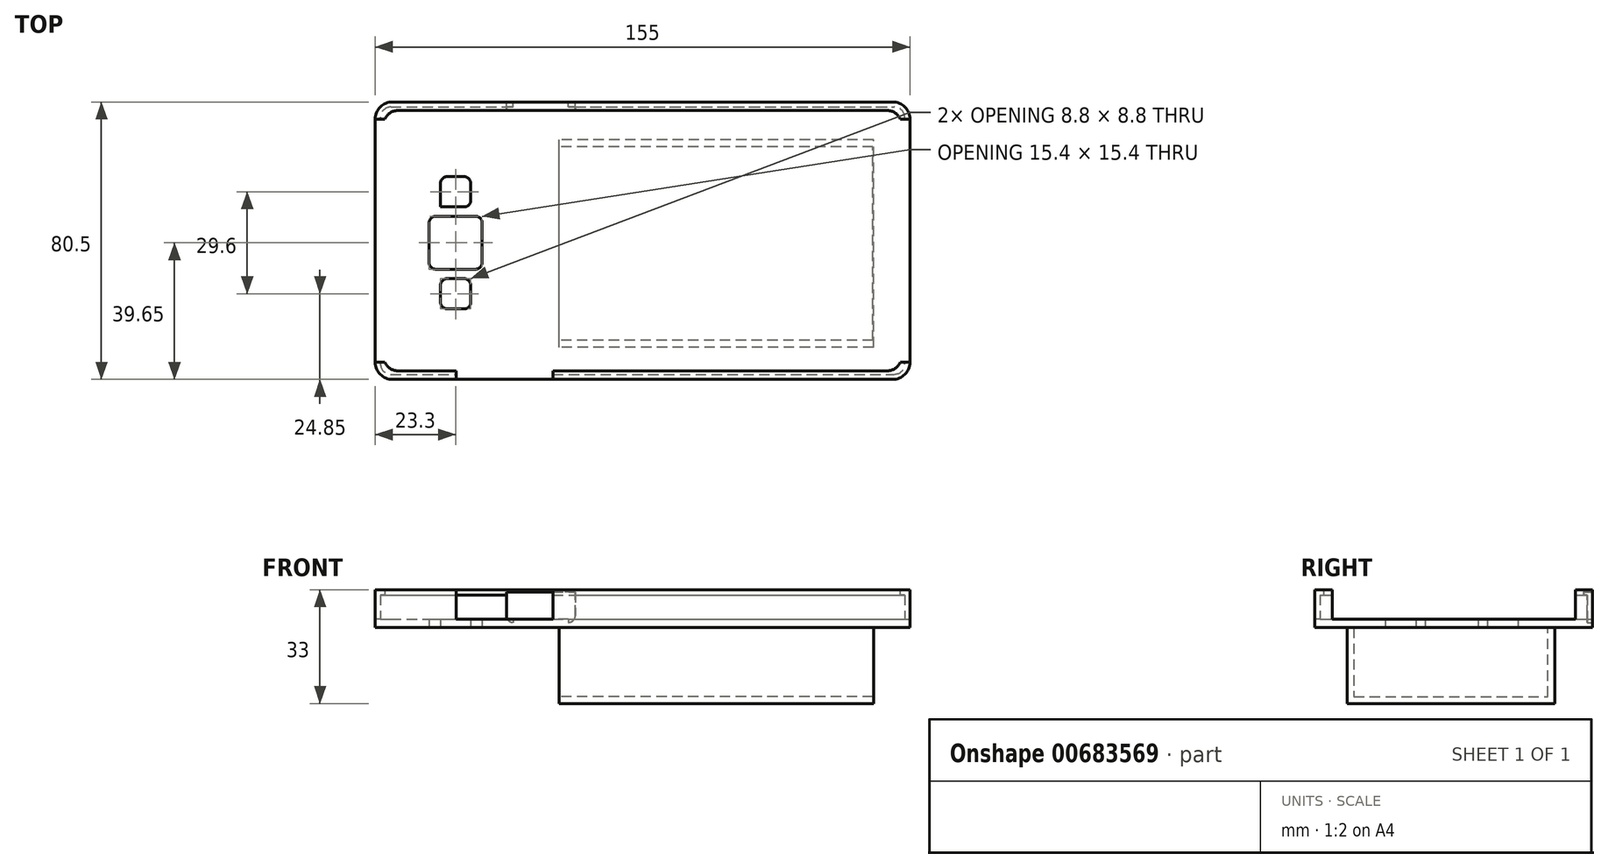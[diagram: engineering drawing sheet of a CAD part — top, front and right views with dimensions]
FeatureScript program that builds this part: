
annotation { "Feature Type Name" : "Feature", "Feature Type Description" : "" }
export const myFeature = defineFeature(function(context is Context, id is Id, definition is map)
    precondition{}
    {
        {
            var Q0;
            Q0=qCreatedBy(makeId("Top.planeOp"),FACE);
            var sketch = newSketch(context, id + "F0", { "sketchPlane" : qUnion([Q0])});
            skLineSegment(sketch, "E0.bottom", {"start": v(0, 0) * mm, "end": v(155, 0) * mm});
            skLineSegment(sketch, "E0.top", {"start": v(0, 80.5) * mm, "end": v(155, 80.5) * mm});
            skLineSegment(sketch, "E0.left", {"start": v(0, 0) * mm, "end": v(0, 80.5) * mm});
            skLineSegment(sketch, "E0.right", {"start": v(155, 0) * mm, "end": v(155, 80.5) * mm});
            skSolve(sketch);
        }
        {
            var Q0;
            Q0=qSketchRegion(id+"F0",true);
            extrude(context, id + "F1", {"entities" : qUnion([Q0]), "depth" : 9.5 * mm, "offsetDistance" : 25 * mm});
        }
        {
            var Q0;
            Q0=makeQuery(id+"F1.opExtrude","CAP_FACE",FACE,{"disambiguationData":[OSD([sQuery(id+"F0.wireOp",EDGE,"E0.bottom"),sQuery(id+"F0.wireOp",EDGE,"E0.top"),sQuery(id+"F0.wireOp",EDGE,"E0.left"),sQuery(id+"F0.wireOp",EDGE,"E0.right")])],"isStart":false});
            shell(context, id + "F2", {"entities" : qUnion([Q0]), "thickness" : 1.5 * mm});
        }
        {
            var Q0;
            Q0=makeQuery(id+"F1.opExtrude","CAP_FACE",FACE,{"disambiguationData":[OSD([sQuery(id+"F0.wireOp",EDGE,"E0.bottom"),sQuery(id+"F0.wireOp",EDGE,"E0.top"),sQuery(id+"F0.wireOp",EDGE,"E0.left"),sQuery(id+"F0.wireOp",EDGE,"E0.right")])],"isStart":false});
            var sketch = newSketch(context, id + "F3", { "sketchPlane" : qUnion([Q0])});
            skLineSegment(sketch, "E1.0", {"start": v(2.5, 78) * mm, "end": v(152.5, 78) * mm});
            skLineSegment(sketch, "E1.1", {"start": v(2.5, 2.5) * mm, "end": v(2.5, 78) * mm});
            skLineSegment(sketch, "E1.2", {"start": v(2.5, 2.5) * mm, "end": v(152.5, 2.5) * mm});
            skLineSegment(sketch, "E1.3", {"start": v(152.5, 2.5) * mm, "end": v(152.5, 78) * mm});
            skSolve(sketch);
        }
        {
            var Q0;
            Q0=makeQuery(id+"F3.imprint","IMPRINT",FACE,{"disambiguationData":[TD([[makeQuery(id+"F3.imprint","IMPRINT",EDGE,{"derivedFrom":sQuery(id+"F3.wireOp",EDGE,"E1.0")}),1.0]])]});
            var Q1;
            {var subQ6=sQuery(id+"F0.wireOp",EDGE,"E0.bottom");var subQ7=makeQuery(id+"F1.opExtrude","CAP_EDGE",EDGE,{"disambiguationData":[OSD([subQ6])],"isStart":false});Q1=makeQuery(id+"F3.imprint","IMPRINT",FACE,{"disambiguationData":[TD([[makeQuery(id+"F3.imprint","IMPRINT",EDGE,{"derivedFrom":subQ7}),1.0]])]});}
            extrude(context, id + "F4", {"entities" : qUnion([Q0, Q1]), "operationType" : NewBodyOperationType.ADD, "depth" : 1.5 * mm, "offsetDistance" : 25 * mm});
        }
        {
            var Q0;
            {var subQ0=sQuery(id+"F0.wireOp",EDGE,"E0.top");Q0=makeQuery(id+"F4.boolean.opBoolean","MERGE",FACE,{"derivedFrom":[makeQuery(id+"F1.opExtrude","SWEPT_FACE",FACE,{"disambiguationData":[OSD([subQ0])]}),makeQuery(id+"F4.opExtrude","SWEPT_FACE",FACE,{"disambiguationData":[OSD([subQ0])]})]});}
            var sketch = newSketch(context, id + "F5", { "sketchPlane" : qUnion([Q0])});
            skLineSegment(sketch, "E2.bottom", {"start": v(-58, 10.3) * mm, "end": v(-38, 10.3) * mm});
            skLineSegment(sketch, "E2.top", {"start": v(-58, 1.5) * mm, "end": v(-38, 1.5) * mm});
            skLineSegment(sketch, "E2.left", {"start": v(-58, 10.3) * mm, "end": v(-58, 1.5) * mm});
            skLineSegment(sketch, "E2.right", {"start": v(-38, 10.3) * mm, "end": v(-38, 1.5) * mm});
            skSolve(sketch);
        }
        {
            var Q0;
            Q0=makeQuery(id+"F5.imprint","IMPRINT",FACE,{"disambiguationData":[TD([[makeQuery(id+"F5.imprint","IMPRINT",EDGE,{"derivedFrom":sQuery(id+"F5.wireOp",EDGE,"E2.bottom")}),-1.0]])]});
            extrude(context, id + "F6", {"entities" : qUnion([Q0]), "operationType" : NewBodyOperationType.REMOVE, "endBound" : BoundingType.UP_TO_NEXT, "oppositeDirection" : true, "depth" : 25 * mm, "offsetDistance" : 25 * mm});
        }
        {
            var Q0;
            Q0=makeQuery(id+"F1.opExtrude","CAP_FACE",FACE,{"disambiguationData":[OSD([sQuery(id+"F0.wireOp",EDGE,"E0.bottom"),sQuery(id+"F0.wireOp",EDGE,"E0.top"),sQuery(id+"F0.wireOp",EDGE,"E0.left"),sQuery(id+"F0.wireOp",EDGE,"E0.right")])],"isStart":true});
            var sketch = newSketch(context, id + "F7", { "sketchPlane" : qUnion([Q0])});
            skLineSegment(sketch, "E3.bottom", {"start": v(18.9, -20.45) * mm, "end": v(27.7, -20.45) * mm});
            skLineSegment(sketch, "E3.top", {"start": v(18.9, -29.25) * mm, "end": v(27.7, -29.25) * mm});
            skLineSegment(sketch, "E3.left", {"start": v(18.9, -20.45) * mm, "end": v(18.9, -29.25) * mm});
            skLineSegment(sketch, "E3.right", {"start": v(27.7, -20.45) * mm, "end": v(27.7, -29.25) * mm});
            skLineSegment(sketch, "E4.bottom", {"start": v(15.6, -31.95) * mm, "end": v(31, -31.95) * mm});
            skLineSegment(sketch, "E4.top", {"start": v(15.6, -47.35) * mm, "end": v(31, -47.35) * mm});
            skLineSegment(sketch, "E4.left", {"start": v(15.6, -31.95) * mm, "end": v(15.6, -47.35) * mm});
            skLineSegment(sketch, "E4.right", {"start": v(31, -31.95) * mm, "end": v(31, -47.35) * mm});
            skLineSegment(sketch, "E5.bottom", {"start": v(18.9, -50.05) * mm, "end": v(27.7, -50.05) * mm});
            skLineSegment(sketch, "E5.top", {"start": v(18.9, -58.85) * mm, "end": v(27.7, -58.85) * mm});
            skLineSegment(sketch, "E5.left", {"start": v(18.9, -50.05) * mm, "end": v(18.9, -58.85) * mm});
            skLineSegment(sketch, "E5.right", {"start": v(27.7, -50.05) * mm, "end": v(27.7, -58.85) * mm});
            skLineSegment(sketch, "E6", {"start": v(12.52, -39.65) * mm, "end": v(41, -39.65) * mm});
            skPoint(sketch, "E6.startSnap0", {"position": v(15.6, -39.65) * mm});
            skLineSegment(sketch, "E7", {"start": v(16.62, -24.85) * mm, "end": v(34.64, -24.85) * mm});
            skPoint(sketch, "E7.startSnap0", {"position": v(18.9, -24.85) * mm});
            skLineSegment(sketch, "E8", {"start": v(16.41, -54.45) * mm, "end": v(34.85, -54.45) * mm});
            skPoint(sketch, "E8.startSnap0", {"position": v(18.9, -54.45) * mm});
            skSolve(sketch);
        }
        {
            var Q0;
            {var subQ0=sQuery(id+"F7.wireOp",EDGE,"E3.top");Q0=makeQuery(id+"F7.imprint","IMPRINT",FACE,{"disambiguationData":[TD([[makeQuery(id+"F7.imprint","IMPRINT",EDGE,{"derivedFrom":subQ0}),1.0]])]});}
            var Q1;
            {var subQ0=sQuery(id+"F7.wireOp",EDGE,"E3.bottom");Q1=makeQuery(id+"F7.imprint","IMPRINT",FACE,{"disambiguationData":[TD([[makeQuery(id+"F7.imprint","IMPRINT",EDGE,{"derivedFrom":subQ0}),-1.0]])]});}
            var Q2;
            {var subQ0=sQuery(id+"F7.wireOp",EDGE,"E4.bottom");Q2=makeQuery(id+"F7.imprint","IMPRINT",FACE,{"disambiguationData":[TD([[makeQuery(id+"F7.imprint","IMPRINT",EDGE,{"derivedFrom":subQ0}),-1.0]])]});}
            var Q3;
            {var subQ0=sQuery(id+"F7.wireOp",EDGE,"E4.top");Q3=makeQuery(id+"F7.imprint","IMPRINT",FACE,{"disambiguationData":[TD([[makeQuery(id+"F7.imprint","IMPRINT",EDGE,{"derivedFrom":subQ0}),1.0]])]});}
            var Q4;
            {var subQ0=sQuery(id+"F7.wireOp",EDGE,"E5.bottom");Q4=makeQuery(id+"F7.imprint","IMPRINT",FACE,{"disambiguationData":[TD([[makeQuery(id+"F7.imprint","IMPRINT",EDGE,{"derivedFrom":subQ0}),-1.0]])]});}
            var Q5;
            {var subQ0=sQuery(id+"F7.wireOp",EDGE,"E5.top");Q5=makeQuery(id+"F7.imprint","IMPRINT",FACE,{"disambiguationData":[TD([[makeQuery(id+"F7.imprint","IMPRINT",EDGE,{"derivedFrom":subQ0}),1.0]])]});}
            extrude(context, id + "F8", {"entities" : qUnion([Q0, Q1, Q2, Q3, Q4, Q5]), "operationType" : NewBodyOperationType.REMOVE, "endBound" : BoundingType.UP_TO_NEXT, "oppositeDirection" : true, "depth" : 25 * mm, "offsetDistance" : 25 * mm});
        }
        {
            var Q0;
            Q0=makeQuery(id+"F8.boolean.opBoolean","COPY",EDGE,{"derivedFrom":makeQuery(id+"F8.opExtrude","SWEPT_EDGE",EDGE,{"disambiguationData":[OSD([sQuery(id+"F7.wireOp",EDGE,"E3.top"),sQuery(id+"F7.wireOp",EDGE,"E3.left")])]})});
            var Q1;
            Q1=makeQuery(id+"F8.boolean.opBoolean","COPY",EDGE,{"derivedFrom":makeQuery(id+"F8.opExtrude","SWEPT_EDGE",EDGE,{"disambiguationData":[OSD([sQuery(id+"F7.wireOp",EDGE,"E4.top"),sQuery(id+"F7.wireOp",EDGE,"E4.left")])]})});
            var Q2;
            Q2=makeQuery(id+"F8.boolean.opBoolean","COPY",EDGE,{"derivedFrom":makeQuery(id+"F8.opExtrude","SWEPT_EDGE",EDGE,{"disambiguationData":[OSD([sQuery(id+"F7.wireOp",EDGE,"E5.top"),sQuery(id+"F7.wireOp",EDGE,"E5.left")])]})});
            var Q3;
            Q3=makeQuery(id+"F8.boolean.opBoolean","COPY",EDGE,{"derivedFrom":makeQuery(id+"F8.opExtrude","SWEPT_EDGE",EDGE,{"disambiguationData":[OSD([sQuery(id+"F7.wireOp",EDGE,"E3.bottom"),sQuery(id+"F7.wireOp",EDGE,"E3.left")])]})});
            var Q4;
            Q4=makeQuery(id+"F8.boolean.opBoolean","COPY",EDGE,{"derivedFrom":makeQuery(id+"F8.opExtrude","SWEPT_EDGE",EDGE,{"disambiguationData":[OSD([sQuery(id+"F7.wireOp",EDGE,"E4.bottom"),sQuery(id+"F7.wireOp",EDGE,"E4.left")])]})});
            var Q5;
            Q5=makeQuery(id+"F8.boolean.opBoolean","COPY",EDGE,{"derivedFrom":makeQuery(id+"F8.opExtrude","SWEPT_EDGE",EDGE,{"disambiguationData":[OSD([sQuery(id+"F7.wireOp",EDGE,"E5.bottom"),sQuery(id+"F7.wireOp",EDGE,"E5.right")])]})});
            var Q6;
            Q6=makeQuery(id+"F8.boolean.opBoolean","COPY",EDGE,{"derivedFrom":makeQuery(id+"F8.opExtrude","SWEPT_EDGE",EDGE,{"disambiguationData":[OSD([sQuery(id+"F7.wireOp",EDGE,"E4.bottom"),sQuery(id+"F7.wireOp",EDGE,"E4.right")])]})});
            var Q7;
            Q7=makeQuery(id+"F8.boolean.opBoolean","COPY",EDGE,{"derivedFrom":makeQuery(id+"F8.opExtrude","SWEPT_EDGE",EDGE,{"disambiguationData":[OSD([sQuery(id+"F7.wireOp",EDGE,"E3.bottom"),sQuery(id+"F7.wireOp",EDGE,"E3.right")])]})});
            var Q8;
            Q8=makeQuery(id+"F8.boolean.opBoolean","COPY",EDGE,{"derivedFrom":makeQuery(id+"F8.opExtrude","SWEPT_EDGE",EDGE,{"disambiguationData":[OSD([sQuery(id+"F7.wireOp",EDGE,"E3.top"),sQuery(id+"F7.wireOp",EDGE,"E3.right")])]})});
            var Q9;
            Q9=makeQuery(id+"F8.boolean.opBoolean","COPY",EDGE,{"derivedFrom":makeQuery(id+"F8.opExtrude","SWEPT_EDGE",EDGE,{"disambiguationData":[OSD([sQuery(id+"F7.wireOp",EDGE,"E4.top"),sQuery(id+"F7.wireOp",EDGE,"E4.right")])]})});
            var Q10;
            Q10=makeQuery(id+"F8.boolean.opBoolean","COPY",EDGE,{"derivedFrom":makeQuery(id+"F8.opExtrude","SWEPT_EDGE",EDGE,{"disambiguationData":[OSD([sQuery(id+"F7.wireOp",EDGE,"E5.top"),sQuery(id+"F7.wireOp",EDGE,"E5.right")])]})});
            var Q11;
            Q11=makeQuery(id+"F6.boolean.opBoolean","COPY",EDGE,{"derivedFrom":makeQuery(id+"F6.opExtrude","SWEPT_EDGE",EDGE,{"disambiguationData":[OSD([sQuery(id+"F5.wireOp",EDGE,"E2.top"),sQuery(id+"F5.wireOp",EDGE,"E2.left")])]})});
            var Q12;
            Q12=makeQuery(id+"F6.boolean.opBoolean","COPY",EDGE,{"derivedFrom":makeQuery(id+"F6.opExtrude","SWEPT_EDGE",EDGE,{"disambiguationData":[OSD([sQuery(id+"F5.wireOp",EDGE,"E2.top"),sQuery(id+"F5.wireOp",EDGE,"E2.right")])]})});
            var Q13;
            Q13=makeQuery(id+"Fbyri0PJp8Br0oV_1.boolean.opBoolean","COPY",EDGE,{"derivedFrom":makeQuery(id+"Fbyri0PJp8Br0oV_1.opExtrude","SWEPT_EDGE",EDGE,{"disambiguationData":[OSD([sQuery(id+"FvTYZWZqDNshxX4_1.wireOp",EDGE,"IeMp83hV-Eg84-gsiM-G3zc-KtJ31x0ztoL4.top"),sQuery(id+"FvTYZWZqDNshxX4_1.wireOp",EDGE,"IeMp83hV-Eg84-gsiM-G3zc-KtJ31x0ztoL4.left")])]})});
            var Q14;
            Q14=makeQuery(id+"Fbyri0PJp8Br0oV_1.boolean.opBoolean","COPY",EDGE,{"derivedFrom":makeQuery(id+"Fbyri0PJp8Br0oV_1.opExtrude","SWEPT_EDGE",EDGE,{"disambiguationData":[OSD([sQuery(id+"FvTYZWZqDNshxX4_1.wireOp",EDGE,"IeMp83hV-Eg84-gsiM-G3zc-KtJ31x0ztoL4.top"),sQuery(id+"FvTYZWZqDNshxX4_1.wireOp",EDGE,"IeMp83hV-Eg84-gsiM-G3zc-KtJ31x0ztoL4.right")])]})});
            fillet(context, id + "F9", {"entities" : qUnion([Q0, Q1, Q2, Q3, Q4, Q5, Q6, Q7, Q8, Q9, Q10, Q11, Q12, Q13, Q14]), "radius" : 2 * mm, "tangentPropagation" : true, "allowEdgeOverflow" : false});
        }
        {
            var Q0;
            {var subQ0=sQuery(id+"F0.wireOp",EDGE,"E0.left");var subQ1=sQuery(id+"F0.wireOp",EDGE,"E0.bottom");Q0=makeQuery(id+"F4.boolean.opBoolean","MERGE",EDGE,{"derivedFrom":[makeQuery(id+"F1.opExtrude","SWEPT_EDGE",EDGE,{"disambiguationData":[OSD([subQ1,subQ0])]}),makeQuery(id+"F4.opExtrude","SWEPT_EDGE",EDGE,{"disambiguationData":[OSD([subQ1,subQ0])]})]});}
            var Q1;
            {var subQ0=sQuery(id+"F0.wireOp",EDGE,"E0.left");var subQ1=sQuery(id+"F0.wireOp",EDGE,"E0.top");Q1=makeQuery(id+"F4.boolean.opBoolean","MERGE",EDGE,{"derivedFrom":[makeQuery(id+"F1.opExtrude","SWEPT_EDGE",EDGE,{"disambiguationData":[OSD([subQ1,subQ0])]}),makeQuery(id+"F4.opExtrude","SWEPT_EDGE",EDGE,{"disambiguationData":[OSD([subQ1,subQ0])]})]});}
            var Q2;
            {var subQ0=sQuery(id+"F0.wireOp",EDGE,"E0.right");var subQ1=sQuery(id+"F0.wireOp",EDGE,"E0.bottom");Q2=makeQuery(id+"F4.boolean.opBoolean","MERGE",EDGE,{"derivedFrom":[makeQuery(id+"F1.opExtrude","SWEPT_EDGE",EDGE,{"disambiguationData":[OSD([subQ1,subQ0])]}),makeQuery(id+"F4.opExtrude","SWEPT_EDGE",EDGE,{"disambiguationData":[OSD([subQ1,subQ0])]})]});}
            var Q3;
            {var subQ0=sQuery(id+"F0.wireOp",EDGE,"E0.right");var subQ1=sQuery(id+"F0.wireOp",EDGE,"E0.top");Q3=makeQuery(id+"F4.boolean.opBoolean","MERGE",EDGE,{"derivedFrom":[makeQuery(id+"F1.opExtrude","SWEPT_EDGE",EDGE,{"disambiguationData":[OSD([subQ1,subQ0])]}),makeQuery(id+"F4.opExtrude","SWEPT_EDGE",EDGE,{"disambiguationData":[OSD([subQ1,subQ0])]})]});}
            fillet(context, id + "F10", {"entities" : qUnion([Q0, Q1, Q2, Q3]), "radius" : 5 * mm, "tangentPropagation" : true, "allowEdgeOverflow" : false});
        }
        {
            var Q0;
            Q0=makeQuery(id+"F2.opShell","OFFSET_EDGE",EDGE,{"disambiguationData":[OSD([sQuery(id+"F0.wireOp",EDGE,"E0.top"),sQuery(id+"F0.wireOp",EDGE,"E0.left")])]});
            var Q1;
            Q1=makeQuery(id+"F2.opShell","OFFSET_EDGE",EDGE,{"disambiguationData":[OSD([sQuery(id+"F0.wireOp",EDGE,"E0.bottom"),sQuery(id+"F0.wireOp",EDGE,"E0.left")])]});
            var Q2;
            Q2=makeQuery(id+"F2.opShell","OFFSET_EDGE",EDGE,{"disambiguationData":[OSD([sQuery(id+"F0.wireOp",EDGE,"E0.top"),sQuery(id+"F0.wireOp",EDGE,"E0.right")])]});
            var Q3;
            Q3=makeQuery(id+"F2.opShell","OFFSET_EDGE",EDGE,{"disambiguationData":[OSD([sQuery(id+"F0.wireOp",EDGE,"E0.bottom"),sQuery(id+"F0.wireOp",EDGE,"E0.right")])]});
            fillet(context, id + "F11", {"entities" : qUnion([Q0, Q1, Q2, Q3]), "radius" : 3 * mm, "tangentPropagation" : true, "allowEdgeOverflow" : false});
        }
        {
            var Q0;
            Q0=makeQuery(id+"F4.opExtrude","SWEPT_EDGE",EDGE,{"disambiguationData":[OSD([sQuery(id+"F3.wireOp",EDGE,"E1.0"),sQuery(id+"F3.wireOp",EDGE,"E1.1")])]});
            var Q1;
            Q1=makeQuery(id+"F4.opExtrude","SWEPT_EDGE",EDGE,{"disambiguationData":[OSD([sQuery(id+"F3.wireOp",EDGE,"E1.1"),sQuery(id+"F3.wireOp",EDGE,"E1.2")])]});
            var Q2;
            Q2=makeQuery(id+"F4.opExtrude","SWEPT_EDGE",EDGE,{"disambiguationData":[OSD([sQuery(id+"F3.wireOp",EDGE,"E1.0"),sQuery(id+"F3.wireOp",EDGE,"E1.3")])]});
            var Q3;
            Q3=makeQuery(id+"F4.opExtrude","SWEPT_EDGE",EDGE,{"disambiguationData":[OSD([sQuery(id+"F3.wireOp",EDGE,"E1.2"),sQuery(id+"F3.wireOp",EDGE,"E1.3")])]});
            fillet(context, id + "F12", {"entities" : qUnion([Q0, Q1, Q2, Q3]), "radius" : 4 * mm, "tangentPropagation" : true, "allowEdgeOverflow" : false});
        }
        {
            var Q0;
            {var subQ0=sQuery(id+"F0.wireOp",EDGE,"E0.left");Q0=makeQuery(id+"F4.boolean.opBoolean","MERGE",FACE,{"derivedFrom":[makeQuery(id+"F1.opExtrude","SWEPT_FACE",FACE,{"disambiguationData":[OSD([subQ0])]}),makeQuery(id+"F4.opExtrude","SWEPT_FACE",FACE,{"disambiguationData":[OSD([subQ0])]})]});}
            var sketch = newSketch(context, id + "F13", { "sketchPlane" : qUnion([Q0])});
            skLineSegment(sketch, "E9.bottom", {"start": v(-75.5, 11) * mm, "end": v(-5, 11) * mm});
            skLineSegment(sketch, "E9.top", {"start": v(-75.5, 1.5) * mm, "end": v(-5, 1.5) * mm});
            skLineSegment(sketch, "E9.left", {"start": v(-75.5, 11) * mm, "end": v(-75.5, 1.5) * mm});
            skLineSegment(sketch, "E9.right", {"start": v(-5, 11) * mm, "end": v(-5, 1.5) * mm});
            skSolve(sketch);
        }
        {
            var Q0;
            Q0=qSketchRegion(id+"F13",true);
            extrude(context, id + "F14", {"entities" : qUnion([Q0]), "operationType" : NewBodyOperationType.REMOVE, "endBound" : BoundingType.UP_TO_NEXT, "oppositeDirection" : true, "depth" : 25 * mm, "offsetDistance" : 25 * mm});
        }
        {
            var Q0;
            {var subQ0=sQuery(id+"F0.wireOp",EDGE,"E0.right");Q0=makeQuery(id+"F4.boolean.opBoolean","MERGE",FACE,{"derivedFrom":[makeQuery(id+"F1.opExtrude","SWEPT_FACE",FACE,{"disambiguationData":[OSD([subQ0])]}),makeQuery(id+"F4.opExtrude","SWEPT_FACE",FACE,{"disambiguationData":[OSD([subQ0])]})]});}
            var sketch = newSketch(context, id + "F15", { "sketchPlane" : qUnion([Q0])});
            skLineSegment(sketch, "E10.bottom", {"start": v(5, 11) * mm, "end": v(75.5, 11) * mm});
            skLineSegment(sketch, "E10.top", {"start": v(5, 1.5) * mm, "end": v(75.5, 1.5) * mm});
            skLineSegment(sketch, "E10.left", {"start": v(5, 11) * mm, "end": v(5, 1.5) * mm});
            skLineSegment(sketch, "E10.right", {"start": v(75.5, 11) * mm, "end": v(75.5, 1.5) * mm});
            skSolve(sketch);
        }
        {
            var Q0;
            Q0=makeQuery(id+"F15.imprint","IMPRINT",FACE,{"disambiguationData":[TD([[makeQuery(id+"F15.imprint","IMPRINT",EDGE,{"derivedFrom":sQuery(id+"F15.wireOp",EDGE,"E10.bottom")}),-1.0]])]});
            extrude(context, id + "F16", {"entities" : qUnion([Q0]), "operationType" : NewBodyOperationType.REMOVE, "endBound" : BoundingType.UP_TO_NEXT, "oppositeDirection" : true, "depth" : 25 * mm, "offsetDistance" : 25 * mm});
        }
        {
            var Q0;
            {var subQ0=sQuery(id+"F0.wireOp",EDGE,"E0.bottom");Q0=makeQuery(id+"F4.boolean.opBoolean","MERGE",FACE,{"derivedFrom":[makeQuery(id+"F1.opExtrude","SWEPT_FACE",FACE,{"disambiguationData":[OSD([subQ0])]}),makeQuery(id+"F4.opExtrude","SWEPT_FACE",FACE,{"disambiguationData":[OSD([subQ0])]})]});}
            var sketch = newSketch(context, id + "F17", { "sketchPlane" : qUnion([Q0])});
            skLineSegment(sketch, "E11.bottom", {"start": v(23.5, 11) * mm, "end": v(51.5, 11) * mm});
            skLineSegment(sketch, "E11.top", {"start": v(23.5, 1.5) * mm, "end": v(51.5, 1.5) * mm});
            skLineSegment(sketch, "E11.left", {"start": v(23.5, 11) * mm, "end": v(23.5, 1.5) * mm});
            skLineSegment(sketch, "E11.right", {"start": v(51.5, 11) * mm, "end": v(51.5, 1.5) * mm});
            skSolve(sketch);
        }
        {
            var Q0;
            Q0=makeQuery(id+"F17.imprint","IMPRINT",FACE,{"disambiguationData":[TD([[makeQuery(id+"F17.imprint","IMPRINT",EDGE,{"derivedFrom":sQuery(id+"F17.wireOp",EDGE,"E11.bottom")}),-1.0]])]});
            extrude(context, id + "F18", {"entities" : qUnion([Q0]), "operationType" : NewBodyOperationType.REMOVE, "endBound" : BoundingType.UP_TO_NEXT, "oppositeDirection" : true, "depth" : 25 * mm, "offsetDistance" : 25 * mm});
        }
        {
            var Q0;
            Q0=makeQuery(id+"F18.boolean.opBoolean","MERGE",FACE,{"derivedFrom":[makeQuery(id+"F16.boolean.opBoolean","MERGE",FACE,{"derivedFrom":[makeQuery(id+"F14.boolean.opBoolean","MERGE",FACE,{"derivedFrom":[makeQuery(id+"F6.boolean.opBoolean","MERGE",FACE,{"derivedFrom":[makeQuery(id+"F2.opShell","OFFSET_FACE",FACE,{"disambiguationData":[OSD([sQuery(id+"F0.wireOp",EDGE,"E0.bottom"),sQuery(id+"F0.wireOp",EDGE,"E0.top"),sQuery(id+"F0.wireOp",EDGE,"E0.left"),sQuery(id+"F0.wireOp",EDGE,"E0.right")])]}),makeQuery(id+"F6.opExtrude","SWEPT_FACE",FACE,{"disambiguationData":[OSD([sQuery(id+"F5.wireOp",EDGE,"E2.top")])]})]}),makeQuery(id+"F14.opExtrude","SWEPT_FACE",FACE,{"disambiguationData":[OSD([sQuery(id+"F13.wireOp",EDGE,"E9.top")])]})]}),makeQuery(id+"F16.opExtrude","SWEPT_FACE",FACE,{"disambiguationData":[OSD([sQuery(id+"F15.wireOp",EDGE,"E10.top")])]})]}),makeQuery(id+"F18.opExtrude","SWEPT_FACE",FACE,{"disambiguationData":[OSD([sQuery(id+"F17.wireOp",EDGE,"E11.top")])]})]});
            extrude(context, id + "F19", {"entities" : qUnion([Q0]), "operationType" : NewBodyOperationType.ADD, "depth" : 1 * mm, "offsetDistance" : 25 * mm});
        }
        {
            var Q0;
            Q0=makeQuery(id+"F1.opExtrude","CAP_FACE",FACE,{"disambiguationData":[OSD([sQuery(id+"F0.wireOp",EDGE,"E0.bottom"),sQuery(id+"F0.wireOp",EDGE,"E0.top"),sQuery(id+"F0.wireOp",EDGE,"E0.left"),sQuery(id+"F0.wireOp",EDGE,"E0.right")])],"isStart":true});
            var sketch = newSketch(context, id + "F20", { "sketchPlane" : qUnion([Q0])});
            skLineSegment(sketch, "E12.bottom", {"start": v(144.44, -9.3) * mm, "end": v(53.29, -9.3) * mm});
            skLineSegment(sketch, "E12.top", {"start": v(144.44, -69.52) * mm, "end": v(53.29, -69.52) * mm});
            skLineSegment(sketch, "E12.left", {"start": v(144.44, -9.3) * mm, "end": v(144.44, -69.52) * mm});
            skLineSegment(sketch, "E12.right", {"start": v(53.29, -9.3) * mm, "end": v(53.29, -69.52) * mm});
            skSolve(sketch);
        }
        {
            var Q0;
            Q0=makeQuery(id+"F20.imprint","IMPRINT",FACE,{"disambiguationData":[TD([[makeQuery(id+"F20.imprint","IMPRINT",EDGE,{"derivedFrom":sQuery(id+"F20.wireOp",EDGE,"E12.bottom")}),1.0]])]});
            extrude(context, id + "F21", {"entities" : qUnion([Q0]), "operationType" : NewBodyOperationType.ADD, "depth" : 22 * mm, "offsetDistance" : 25 * mm});
        }
        {
            var Q0;
            Q0=makeQuery(id+"F21.opExtrude","SWEPT_FACE",FACE,{"disambiguationData":[OSD([sQuery(id+"F20.wireOp",EDGE,"E12.right")])]});
            var sketch = newSketch(context, id + "F22", { "sketchPlane" : qUnion([Q0])});
            skLineSegment(sketch, "E13", {"start": v(-9.3, 0) * mm, "end": v(-11.32, 0) * mm});
            skLineSegment(sketch, "E14", {"start": v(-11.32, 0) * mm, "end": v(-11.32, -20) * mm});
            skLineSegment(sketch, "E15", {"start": v(-11.32, -20) * mm, "end": v(-67.52, -20) * mm});
            skLineSegment(sketch, "E16", {"start": v(-67.52, -20) * mm, "end": v(-11.32, -20) * mm});
            skLineSegment(sketch, "E17", {"start": v(-67.52, -20) * mm, "end": v(-67.52, 0) * mm});
            skLineSegment(sketch, "E18", {"start": v(-67.52, 0) * mm, "end": v(-11.32, 0) * mm});
            skLineSegment(sketch, "E19", {"start": v(-11.32, 0) * mm, "end": v(-67.52, 0) * mm});
            skSolve(sketch);
        }
        {
            var Q0;
            Q0=makeQuery(id+"F22.imprint","IMPRINT",FACE,{"disambiguationData":[TD([[makeQuery(id+"F22.imprint","IMPRINT",EDGE,{"derivedFrom":sQuery(id+"F22.wireOp",EDGE,"E14")}),-1.0]])]});
            extrude(context, id + "F23", {"entities" : qUnion([Q0]), "operationType" : NewBodyOperationType.REMOVE, "oppositeDirection" : true, "depth" : 91 * mm, "offsetDistance" : 25 * mm});
        }
    });
